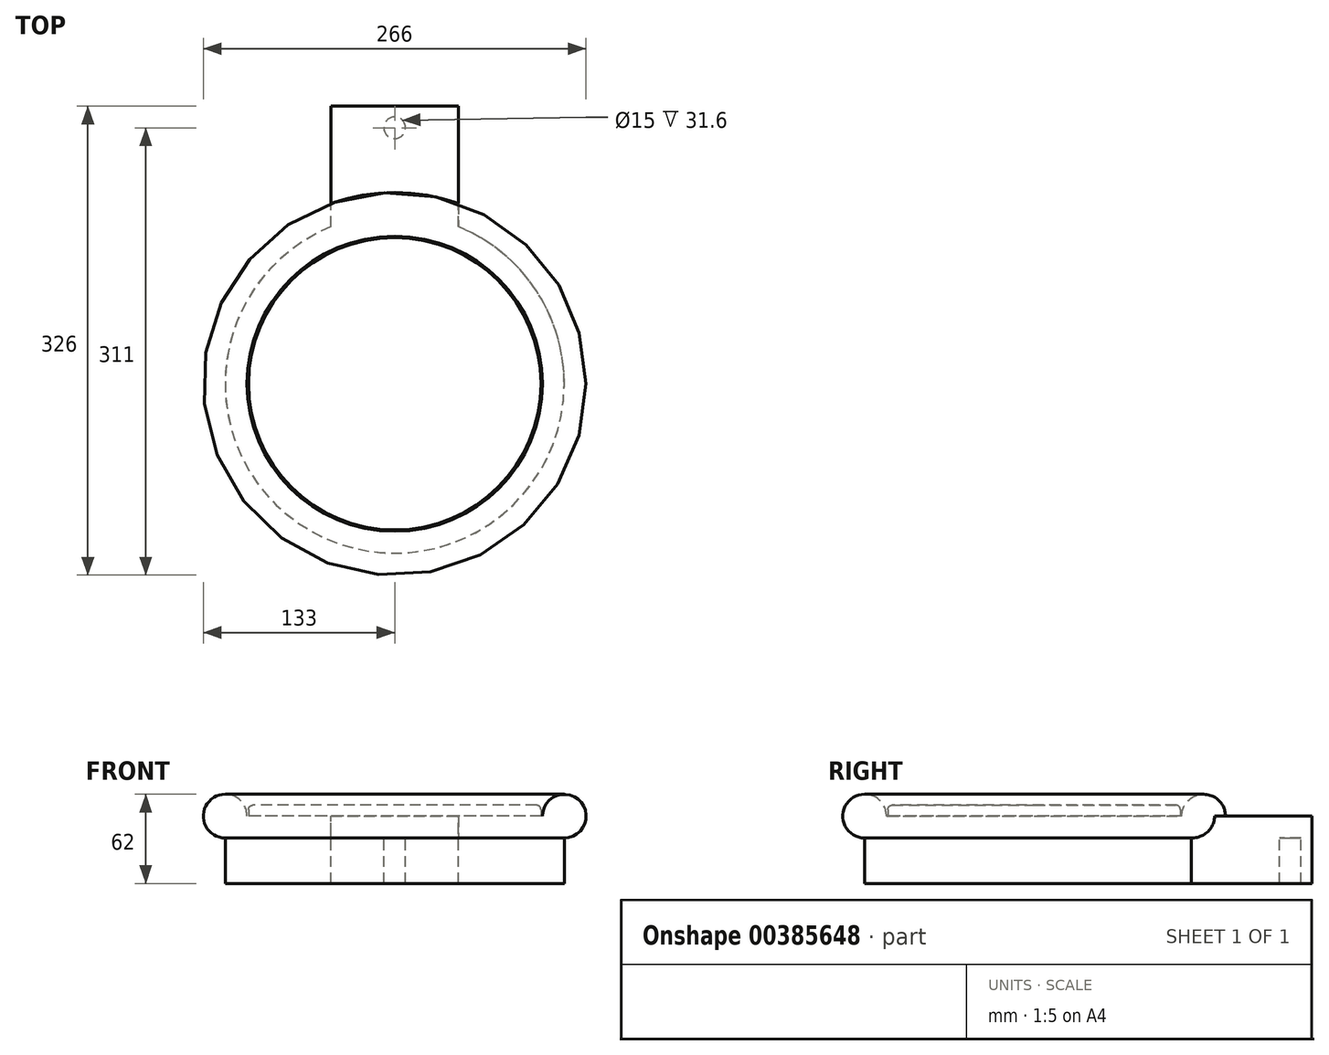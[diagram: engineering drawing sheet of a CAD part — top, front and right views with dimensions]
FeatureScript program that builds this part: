
annotation { "Feature Type Name" : "Feature", "Feature Type Description" : "" }
export const myFeature = defineFeature(function(context is Context, id is Id, definition is map)
    precondition{}
    {
        {
            var Q0;
            Q0=qCreatedBy(makeId("Top.planeOp"),FACE);
            var sketch = newSketch(context, id + "F0", { "sketchPlane" : qUnion([Q0])});
            skCircle(sketch, "E0", {"center": v(0, 0) * mm, "radius": 133 * mm});
            skCircle(sketch, "E1", {"center": v(0, 0) * mm, "radius": 117.8 * mm});
            skCircle(sketch, "E2", {"center": v(0, 0) * mm, "radius": 102.6 * mm});
            skCircle(sketch, "E3", {"center": v(0, 0) * mm, "radius": 101.6 * mm});
            skLineSegment(sketch, "E4.top", {"start": v(-44.33, 193) * mm, "end": v(44.33, 193) * mm});
            skLineSegment(sketch, "E4.left", {"start": v(-44.33, 109.14) * mm, "end": v(-44.33, 193) * mm});
            skLineSegment(sketch, "E4.right", {"start": v(44.33, 109.14) * mm, "end": v(44.33, 193) * mm});
            skLineSegment(sketch, "E5", {"start": v(0, 0) * mm, "end": v(0, -133) * mm, "construction": true});
            skLineSegment(sketch, "E6", {"start": v(0, -102.6) * mm, "end": v(0, -117.8) * mm, "construction": true});
            skLineSegment(sketch, "E7", {"start": v(-6.7, -117.8) * mm, "end": v(6.7, -117.8) * mm, "construction": true});
            skCircle(sketch, "E8", {"center": v(0, 178) * mm, "radius": 7.5 * mm});
            skSolve(sketch);
        }
        {
            assignVariable(context, id + "F1", {"name" : "raio", "anyValue" : 15.2});
        }
        {
            assignVariable(context, id + "F2", {"name" : "alt", "anyValue" : 62 - 2 * 15.2});
        }
        {
            var Q0;
            {var subQ5=sQuery(id+"F0.wireOp",EDGE,"E4.top");Q0=makeQuery(id+"F0.imprint","IMPRINT",FACE,{"disambiguationData":[TD([[makeQuery(id+"F0.imprint","IMPRINT",EDGE,{"derivedFrom":subQ5}),-1.0]])]});}
            var Q1;
            {var subQ0=sQuery(id+"F0.wireOp",EDGE,"E4.left");var subQ1=sQuery(id+"F0.wireOp",EDGE,"E0");var subQ2=makeQuery(id+"F0.imprint","INTERSECT",VERTEX,{"derivedFrom":[subQ1,subQ0]});Q1=makeQuery(id+"F0.imprint","IMPRINT",FACE,{"disambiguationData":[TD([[makeQuery(id+"F0.imprint","IMPRINT",EDGE,{"disambiguationData":[TD([[subQ2,1.0]])],"derivedFrom":subQ1}),1.0]])]});}
            var Q2;
            Q2=makeQuery(id+"F0.imprint","IMPRINT",FACE,{"disambiguationData":[TD([[makeQuery(id+"F0.imprint","IMPRINT",EDGE,{"derivedFrom":sQuery(id+"F0.wireOp",EDGE,"E2")}),-1.0]])]});
            var Q3;
            Q3=makeQuery(id+"F0.imprint","IMPRINT",FACE,{"disambiguationData":[TD([[makeQuery(id+"F0.imprint","IMPRINT",EDGE,{"derivedFrom":sQuery(id+"F0.wireOp",EDGE,"E2")}),1.0]])]});
            var Q4;
            Q4=makeQuery(id+"F0.imprint","IMPRINT",FACE,{"disambiguationData":[TD([[makeQuery(id+"F0.imprint","IMPRINT",EDGE,{"derivedFrom":sQuery(id+"F0.wireOp",EDGE,"E3")}),1.0]])]});
            extrude(context, id + "F3", {"entities" : qUnion([Q0, Q1, Q2, Q3, Q4]), "oppositeDirection" : true, "depth" : (getVariable(context, 'alt')) * mm});
        }
        {
            var Q0;
            {var subQ0=sQuery(id+"F0.wireOp",EDGE,"E4.left");var subQ1=sQuery(id+"F0.wireOp",EDGE,"E0");var subQ2=makeQuery(id+"F0.imprint","INTERSECT",VERTEX,{"derivedFrom":[subQ1,subQ0]});Q0=makeQuery(id+"F0.imprint","IMPRINT",FACE,{"disambiguationData":[TD([[makeQuery(id+"F0.imprint","IMPRINT",EDGE,{"disambiguationData":[TD([[subQ2,-1.0]])],"derivedFrom":subQ1}),1.0]])]});}
            var Q1;
            Q1=makeQuery(id+"F0.imprint","IMPRINT",FACE,{"disambiguationData":[TD([[makeQuery(id+"F0.imprint","IMPRINT",EDGE,{"derivedFrom":sQuery(id+"F0.wireOp",EDGE,"E2")}),-1.0]])]});
            var Q2;
            Q2=makeQuery(id+"F0.imprint","IMPRINT",FACE,{"disambiguationData":[TD([[makeQuery(id+"F0.imprint","IMPRINT",EDGE,{"derivedFrom":sQuery(id+"F0.wireOp",EDGE,"E2")}),1.0]])]});
            var Q3;
            Q3=makeQuery(id+"F0.imprint","IMPRINT",FACE,{"disambiguationData":[TD([[makeQuery(id+"F0.imprint","IMPRINT",EDGE,{"derivedFrom":sQuery(id+"F0.wireOp",EDGE,"E3")}),1.0]])]});
            var Q4;
            {var subQ0=sQuery(id+"F0.wireOp",EDGE,"E4.left");var subQ1=sQuery(id+"F0.wireOp",EDGE,"E0");var subQ2=makeQuery(id+"F0.imprint","INTERSECT",VERTEX,{"derivedFrom":[subQ1,subQ0]});Q4=makeQuery(id+"F0.imprint","IMPRINT",FACE,{"disambiguationData":[TD([[makeQuery(id+"F0.imprint","IMPRINT",EDGE,{"disambiguationData":[TD([[subQ2,1.0]])],"derivedFrom":subQ1}),1.0]])]});}
            var Q5;
            {var subQ5=sQuery(id+"F0.wireOp",EDGE,"E4.top");Q5=makeQuery(id+"F0.imprint","IMPRINT",FACE,{"disambiguationData":[TD([[makeQuery(id+"F0.imprint","IMPRINT",EDGE,{"derivedFrom":subQ5}),-1.0]])]});}
            var Q6;
            {var subQ0=sQuery(id+"F0.wireOp",EDGE,"E8");var subQ1=sQuery(id+"F0.wireOp",EDGE,"E0");var subQ2=makeQuery(id+"F0.imprint","INTERSECT",VERTEX,{"disambiguationData":[OD(0.0)],"derivedFrom":[subQ1,subQ0]});Q6=makeQuery(id+"F0.imprint","IMPRINT",FACE,{"disambiguationData":[TD([[makeQuery(id+"F0.imprint","IMPRINT",EDGE,{"disambiguationData":[TD([[subQ2,-1.0]])],"derivedFrom":subQ1}),1.0]])]});}
            var Q7;
            {var subQ0=sQuery(id+"F0.wireOp",EDGE,"E8");var subQ1=sQuery(id+"F0.wireOp",EDGE,"E0");var subQ2=makeQuery(id+"F0.imprint","INTERSECT",VERTEX,{"disambiguationData":[OD(0.0)],"derivedFrom":[subQ1,subQ0]});Q7=makeQuery(id+"F0.imprint","IMPRINT",FACE,{"disambiguationData":[TD([[makeQuery(id+"F0.imprint","IMPRINT",EDGE,{"disambiguationData":[TD([[subQ2,-1.0]])],"derivedFrom":subQ1}),-1.0]])]});}
            var Q8;
            Q8=makeQuery(id+"F0.imprint","IMPRINT",FACE,{"disambiguationData":[TD([[makeQuery(id+"F0.imprint","IMPRINT",EDGE,{"derivedFrom":sQuery(id+"F0.wireOp",EDGE,"E8")}),1.0]])]});
            extrude(context, id + "F4", {"entities" : qUnion([Q0, Q1, Q2, Q3, Q4, Q5, Q6, Q7, Q8]), "operationType" : NewBodyOperationType.ADD, "depth" : (getVariable(context, 'raio')) * mm});
        }
        {
            var Q0;
            {var subQ0=sQuery(id+"F0.wireOp",EDGE,"E4.left");var subQ1=sQuery(id+"F0.wireOp",EDGE,"E0");var subQ2=makeQuery(id+"F0.imprint","INTERSECT",VERTEX,{"derivedFrom":[subQ1,subQ0]});Q0=makeQuery(id+"F0.imprint","IMPRINT",FACE,{"disambiguationData":[TD([[makeQuery(id+"F0.imprint","IMPRINT",EDGE,{"disambiguationData":[TD([[subQ2,-1.0]])],"derivedFrom":subQ1}),1.0]])]});}
            var Q1;
            Q1=makeQuery(id+"F0.imprint","IMPRINT",FACE,{"disambiguationData":[TD([[makeQuery(id+"F0.imprint","IMPRINT",EDGE,{"derivedFrom":sQuery(id+"F0.wireOp",EDGE,"E2")}),-1.0]])]});
            var Q2;
            {var subQ0=sQuery(id+"F0.wireOp",EDGE,"E4.left");var subQ1=sQuery(id+"F0.wireOp",EDGE,"E0");var subQ2=makeQuery(id+"F0.imprint","INTERSECT",VERTEX,{"derivedFrom":[subQ1,subQ0]});Q2=makeQuery(id+"F0.imprint","IMPRINT",FACE,{"disambiguationData":[TD([[makeQuery(id+"F0.imprint","IMPRINT",EDGE,{"disambiguationData":[TD([[subQ2,1.0]])],"derivedFrom":subQ1}),1.0]])]});}
            var Q3;
            {var subQ0=sQuery(id+"F0.wireOp",EDGE,"E8");var subQ1=sQuery(id+"F0.wireOp",EDGE,"E0");var subQ2=makeQuery(id+"F0.imprint","INTERSECT",VERTEX,{"disambiguationData":[OD(0.0)],"derivedFrom":[subQ1,subQ0]});Q3=makeQuery(id+"F0.imprint","IMPRINT",FACE,{"disambiguationData":[TD([[makeQuery(id+"F0.imprint","IMPRINT",EDGE,{"disambiguationData":[TD([[subQ2,-1.0]])],"derivedFrom":subQ1}),1.0]])]});}
            extrude(context, id + "F5", {"entities" : qUnion([Q0, Q1, Q2, Q3]), "operationType" : NewBodyOperationType.ADD, "depth" : (2 * getVariable(context, 'raio')) * mm, "hasSecondDirection" : true, "secondDirectionOppositeDirection" : false, "secondDirectionDepth" : (getVariable(context, 'raio')) * mm});
        }
        {
            var Q0;
            Q0=makeQuery(id+"F5.opExtrude","CAP_EDGE",EDGE,{"disambiguationData":[OSD([sQuery(id+"F0.wireOp",EDGE,"E0")])],"isStart":false});
            var Q1;
            Q1=makeQuery(id+"F5.opExtrude","CAP_EDGE",EDGE,{"disambiguationData":[OSD([sQuery(id+"F0.wireOp",EDGE,"E2")])],"isStart":false});
            var Q2;
            Q2=makeQuery(id+"F4.opExtrude","CAP_EDGE",EDGE,{"disambiguationData":[OSD([sQuery(id+"F0.wireOp",EDGE,"E0")])],"isStart":true});
            fillet(context, id + "F6", {"entities" : qUnion([Q0, Q1, Q2]), "radius" : (getVariable(context, 'raio')) * mm, "tangentPropagation" : true, "allowEdgeOverflow" : false});
        }
        {
            var Q0;
            Q0=makeQuery(id+"F0.imprint","IMPRINT",FACE,{"disambiguationData":[TD([[makeQuery(id+"F0.imprint","IMPRINT",EDGE,{"derivedFrom":sQuery(id+"F0.wireOp",EDGE,"E3")}),1.0]])]});
            extrude(context, id + "F7", {"entities" : qUnion([Q0]), "depth" : 1.5 * (getVariable(context, 'raio')) * mm, "hasSecondDirection" : true, "secondDirectionOppositeDirection" : false, "secondDirectionDepth" : (getVariable(context, 'raio')) * mm});
        }
        {
            var Q0;
            Q0=makeQuery(id+"F7.opExtrude","CAP_EDGE",EDGE,{"disambiguationData":[OSD([sQuery(id+"F0.wireOp",EDGE,"E3")])],"isStart":false});
            fillet(context, id + "F8", {"entities" : qUnion([Q0]), "radius" : 3 * mm, "tangentPropagation" : true, "allowEdgeOverflow" : false});
        }
    });
